# Revit family: Haworth_Maari_Chair_StarBase_WithTablet NEW
name_source: partatom
category: Furniture
units: mm (PartAtom-declared; Revit-internal decimal feet)

## family parameters
Always vertical = Yes
Cut with Voids When Loaded = No
OmniClass Number = 23.40.70.14.64.21
OmniClass Title = Systems Furniture
Room Calculation Point = No
Shared = No
Work Plane-Based = No

## types (2) — shared parameters
Actual Depth = 28 1/2"
Actual Height = 32"
Actual Width = 28 1/2"
Arm Cap Finish = Haworth _ Polymer _ Water TR-1W
Assembly Code = E2020200
Manufacturer = Haworth
Model = Haworth - Maari
Revision Number = 3
Seat Pan Finish = Haworth _ Paint _ Black
Size = Verify Final Dim. w/ Haworth
Sustainability Info = https://www.haworth.com
URL = https://www.haworth.com
URL - Product = https://www.haworth.com
Warranty = https://cdn.shopify.com

## per-type parameters (varying)
| type | Description | With Arms |
| S75 - Five Star Base - With Arms | Haworth - Maari - Chair - Five Star Base - With Arms | Yes |
| S75 - Five Star Base - No Arms | Haworth - Maari - Chair - Five Star Base - No Arms | No |

## geometry (parser evidence)
native form markers: Sweep x14
no freeform markers — native parametric forms only
